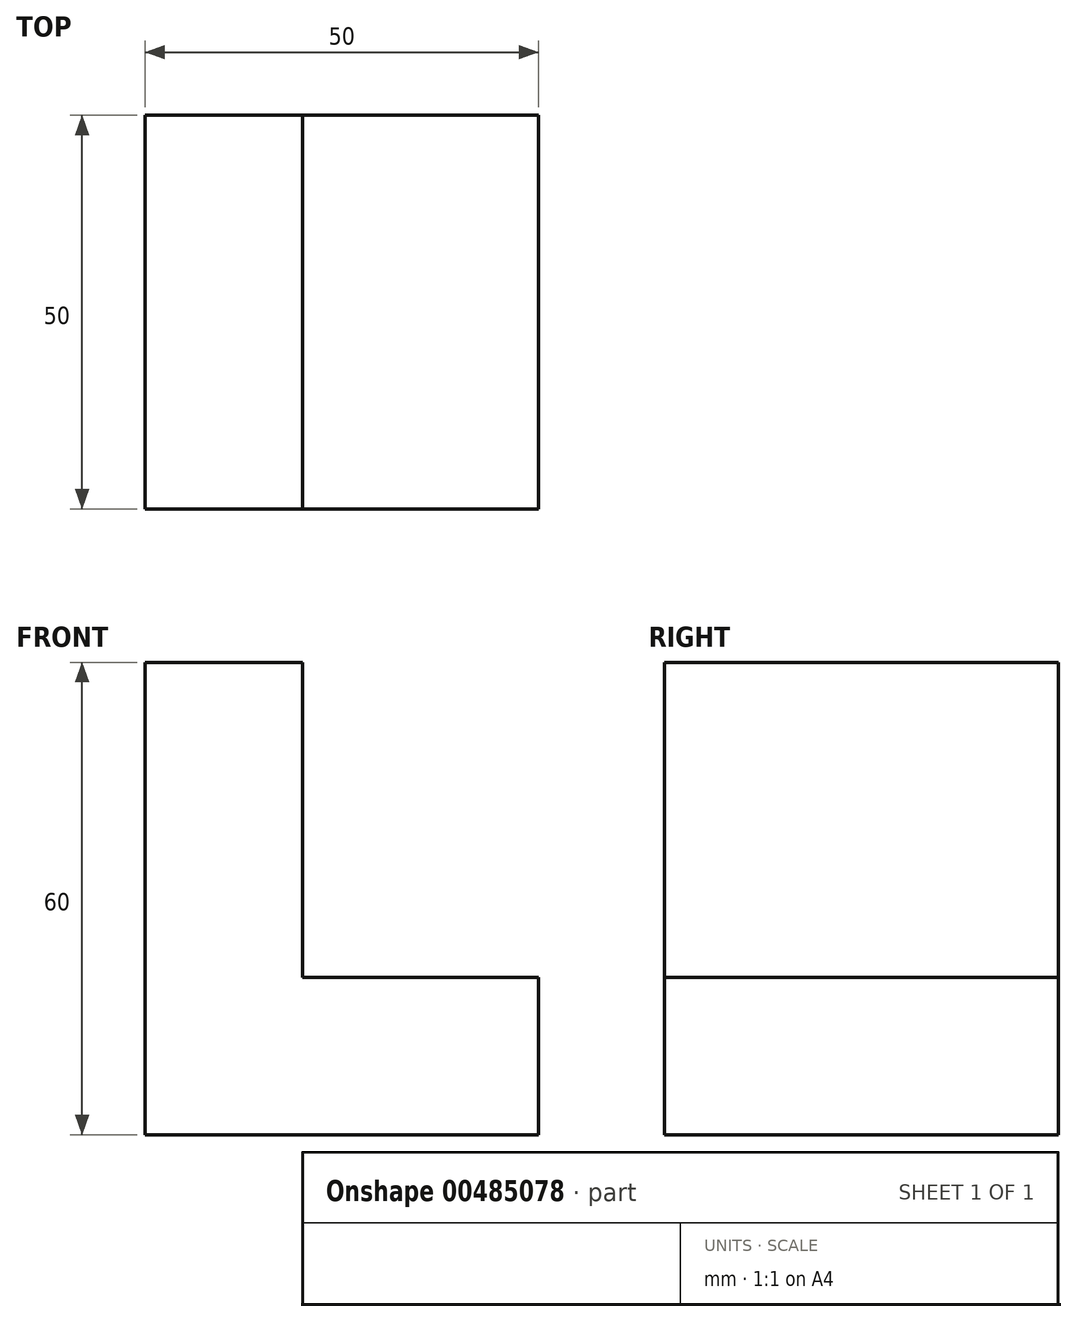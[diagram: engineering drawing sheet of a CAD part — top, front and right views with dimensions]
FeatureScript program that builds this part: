
annotation { "Feature Type Name" : "Feature", "Feature Type Description" : "" }
export const myFeature = defineFeature(function(context is Context, id is Id, definition is map)
    precondition{}
    {
        {
            var Q0;
            Q0=qCreatedBy(makeId("Front.planeOp"),FACE);
            var sketch = newSketch(context, id + "F0", { "sketchPlane" : qUnion([Q0])});
            skLineSegment(sketch, "E0", {"start": v(0, 0) * mm, "end": v(0, 60) * mm});
            skLineSegment(sketch, "E1", {"start": v(0, 60) * mm, "end": v(20, 60) * mm});
            skLineSegment(sketch, "E2", {"start": v(20, 60) * mm, "end": v(20, 20) * mm});
            skLineSegment(sketch, "E3", {"start": v(20, 20) * mm, "end": v(50, 20) * mm});
            skLineSegment(sketch, "E4", {"start": v(50, 20) * mm, "end": v(50, 0) * mm});
            skLineSegment(sketch, "E5", {"start": v(50, 0) * mm, "end": v(0, 0) * mm});
            skSolve(sketch);
        }
        {
            var Q0;
            Q0 = qSketchRegion(id + "F0", true);
            extrude(context, id + "F1", {"entities" : qUnion([Q0]), "depth" : 50 * mm});
        }
    });
